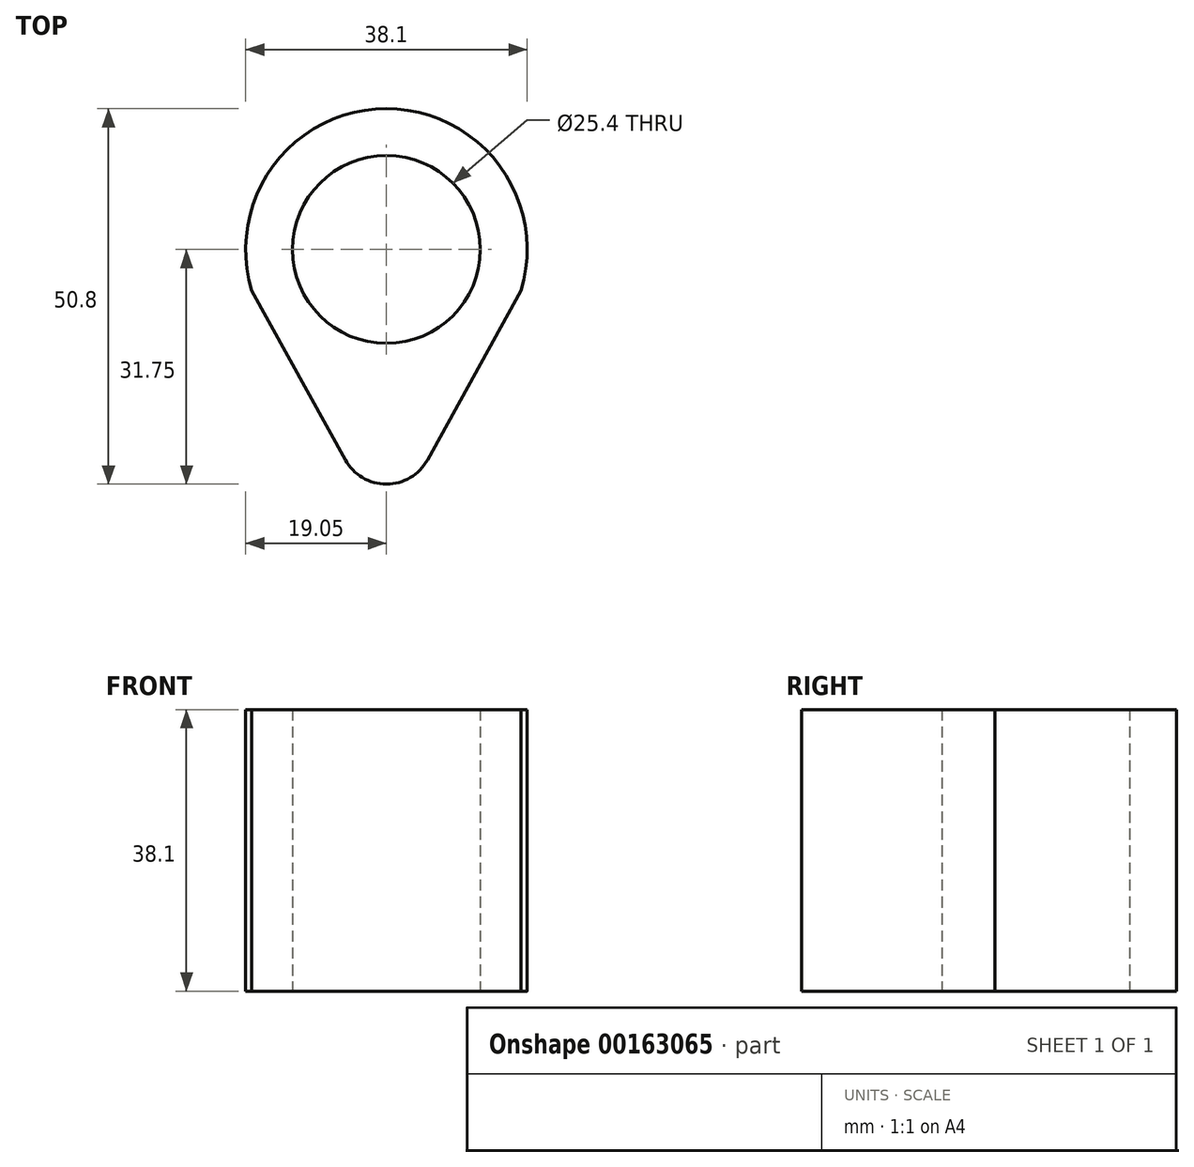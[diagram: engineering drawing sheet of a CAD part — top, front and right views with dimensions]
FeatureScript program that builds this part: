
annotation { "Feature Type Name" : "Feature", "Feature Type Description" : "" }
export const myFeature = defineFeature(function(context is Context, id is Id, definition is map)
    precondition{}
    {
        {
            var Q0;
            Q0=qCreatedBy(makeId("Top.planeOp"),FACE);
            var sketch = newSketch(context, id + "F0", { "sketchPlane" : qUnion([Q0])});
            skCircle(sketch, "E0", {"center": v(0, 0) * mm, "radius": 12.7 * mm});
            skArc(sketch, "E1", {"start": v(18.22, -5.57) * mm, "mid": v(0, 19.05) * mm, "end": v(-18.22, -5.57) * mm});
            skArc(sketch, "E2", {"start": v(-5.56, -28.47) * mm, "mid": v(0, -31.75) * mm, "end": v(5.56, -28.47) * mm});
            skLineSegment(sketch, "E3", {"start": v(18.22, -5.57) * mm, "end": v(5.56, -28.47) * mm});
            skLineSegment(sketch, "E4", {"start": v(-18.22, -5.57) * mm, "end": v(-5.56, -28.47) * mm});
            skSolve(sketch);
        }
        {
            var Q0;
            Q0=makeQuery(id+"F0.imprint","IMPRINT",FACE,{"disambiguationData":[TD([[makeQuery(id+"F0.imprint","IMPRINT",EDGE,{"derivedFrom":sQuery(id+"F0.wireOp",EDGE,"E0")}),-1.0]])]});
            extrude(context, id + "F1", {"entities" : qUnion([Q0]), "depth" : 38.1 * mm});
        }
    });
